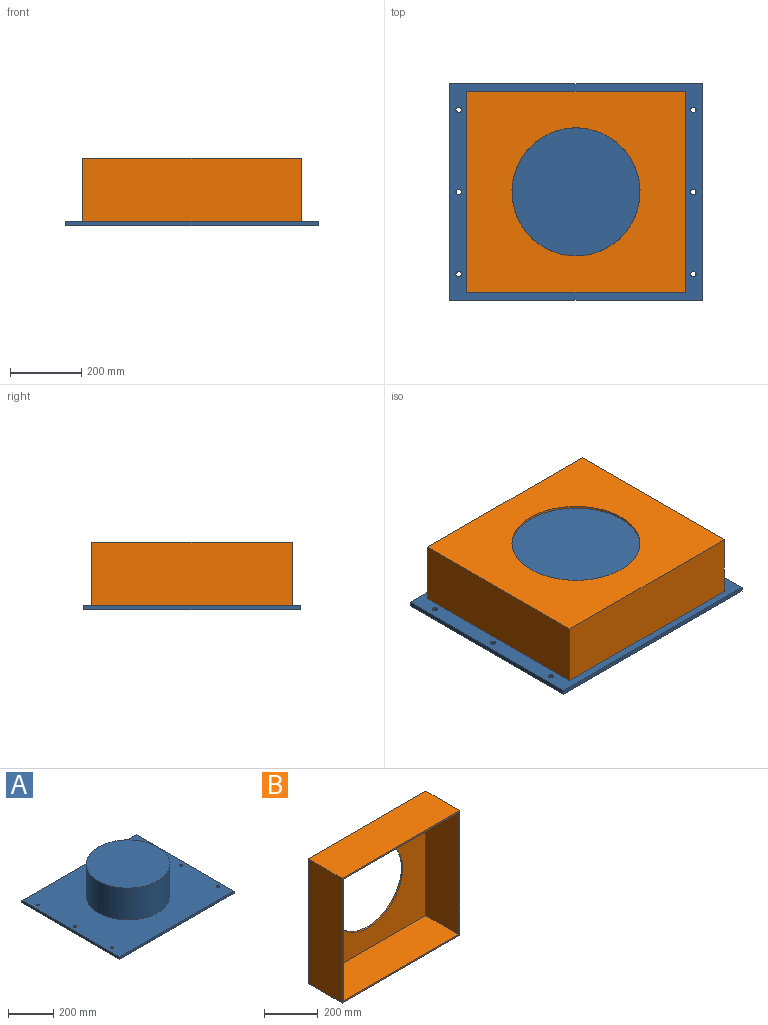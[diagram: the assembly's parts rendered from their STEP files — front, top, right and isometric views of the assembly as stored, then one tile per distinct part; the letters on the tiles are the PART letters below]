
ASSEMBLY  parts=2 mates=1
PART A: 14 faces, bbox 711.2x609.6x184.2 mm
  f0: plane 609.6x12.7mm, normal (-1,0,0), area 7741.9mm2, adj f1,f3,f4,f5
  f1: plane 711.2x12.7mm, normal (0,-1,0), area 9032.2mm2, adj f0,f2,f4,f5
  f2: plane 609.6x12.7mm, normal (1,0,0), area 7741.9mm2, adj f1,f3,f4,f5
  f3: plane 711.2x12.7mm, normal (0,1,0), area 9032.2mm2, adj f0,f2,f4,f5
  f4: plane 711.2x609.6mm, normal (0,0,1), area 325940.3mm2, adj f0,f1,f2,f3,f6,f8,f9,f10
  f5: plane 711.2x609.6mm, normal (0,0,-1), area 432475.5mm2, adj f0,f1,f2,f3,f8,f9,f10,f11
  f6: cylinder r=184.15mm len=368.3mm, axis (0,0,-1), area 198376mm2, adj f4,f7
  f7: plane 368.3x368.3mm, normal (0,0,1), area 106535.2mm2, adj f6
  f8: cylinder r=7.54mm len=15.08mm, axis (0,0,1), area 601.8mm2, adj f4,f5
  f9: cylinder r=7.54mm len=15.08mm, axis (0,0,1), area 601.8mm2, adj f4,f5
  f10: cylinder r=7.54mm len=15.08mm, axis (0,0,1), area 601.8mm2, adj f4,f5
  f11: cylinder r=7.54mm len=15.08mm, axis (0,0,1), area 601.8mm2, adj f4,f5
  f12: cylinder r=7.54mm len=15.08mm, axis (0,0,1), area 601.8mm2, adj f4,f5
  f13: cylinder r=7.54mm len=15.08mm, axis (0,0,1), area 601.8mm2, adj f4,f5
PART B: 12 faces, bbox 616x177.8x565.2 mm
  f0: plane 615.95x565.15mm, normal (0,-1,0), area 14838.7mm2, adj f1,f2,f3,f4,f6,f7,f8,f9
  f1: plane 565.15x177.8mm, normal (-1,0,0), area 100483.7mm2, adj f0,f2,f4,f5
  f2: plane 615.95x177.8mm, normal (0,0,-1), area 109515.9mm2, adj f0,f1,f3,f5
  f3: plane 565.15x177.8mm, normal (1,0,0), area 100483.7mm2, adj f0,f2,f4,f5
  f4: plane 615.95x177.8mm, normal (0,0,1), area 109515.9mm2, adj f0,f1,f3,f5
  f5: plane 615.95x565.15mm, normal (0,1,0), area 246111.4mm2, adj f1,f2,f3,f4,f11
  f6: plane 552.45x171.45mm, normal (1,0,0), area 94717.6mm2, adj f0,f7,f9,f10
  f7: plane 603.25x171.45mm, normal (0,0,1), area 103427.2mm2, adj f0,f6,f8,f10
  f8: plane 552.45x171.45mm, normal (-1,0,0), area 94717.6mm2, adj f0,f7,f9,f10
  f9: plane 603.25x171.45mm, normal (0,0,-1), area 103427.2mm2, adj f0,f6,f8,f10
  f10: plane 603.25x552.45mm, normal (0,-1,0), area 231272.8mm2, adj f6,f7,f8,f9,f11
  f11: cylinder r=180.18mm len=360.36mm, axis (0,1,0), area 7188.9mm2, adj f5,f10
PLACE A rot(axis=(1,0,0),0deg) t=(177.63,150.69,218.89)mm
PLACE B rot(axis=(1,0,0),90deg) t=(177.63,150.69,408.98)mm
MATE slider A.f6 <-> B.f11  axis (0,0,1) through (177.63,150.69,403.04)mm
